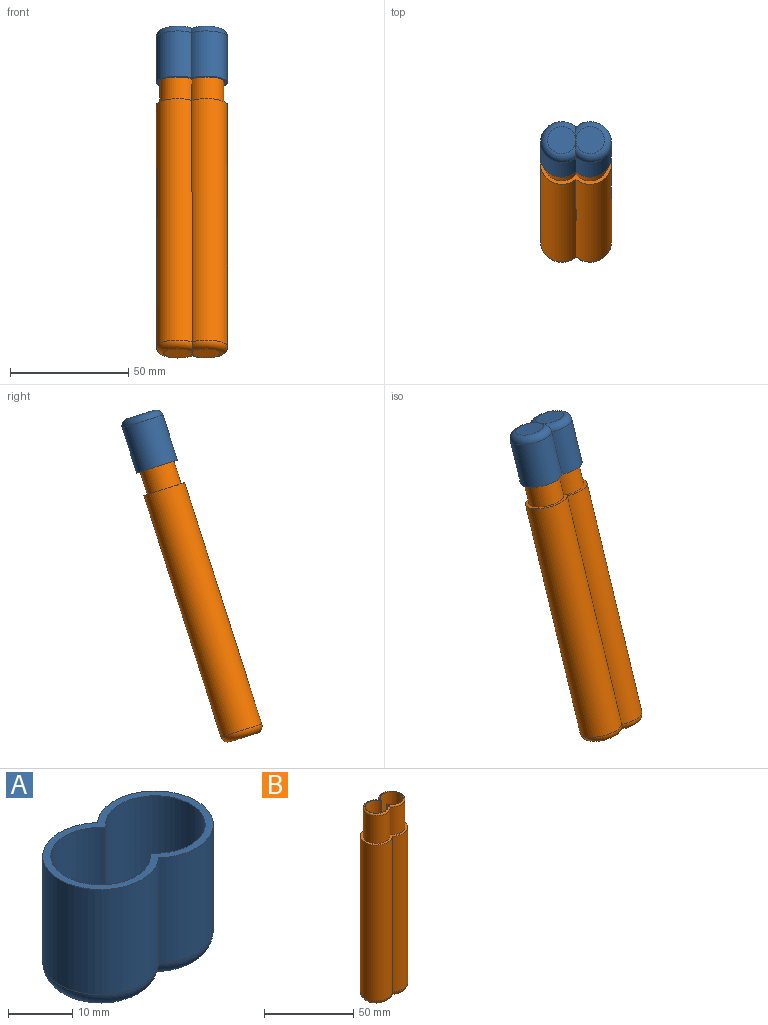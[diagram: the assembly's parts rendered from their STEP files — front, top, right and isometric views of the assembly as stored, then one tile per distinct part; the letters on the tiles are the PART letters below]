
ASSEMBLY  parts=2 mates=1
PART A: 10 faces, bbox 31.5x19.5x23 mm
  f0: plane 12x12mm, normal (0,0,-1), area 113.1mm2, adj f9
  f1: cylinder r=9mm len=20mm, axis (0,0,-1), area 828.2mm2, adj f2,f3,f9
  f2: cylinder r=9mm len=20mm, axis (0,0,-1), area 828.2mm2, adj f1,f3,f8
  f3: plane 30x18mm, normal (0,0,1), area 101.2mm2, adj f1,f2,f5,f6
  f4: plane 12x12mm, normal (0,0,-1), area 113.1mm2, adj f8
  f5: cylinder r=7.73mm len=20.5mm, axis (0,0,1), area 779.2mm2, adj f3,f6,f7
  f6: cylinder r=7.73mm len=20.5mm, axis (0,0,1), area 779.2mm2, adj f3,f5,f7
  f7: plane 27.45x15.45mm, normal (0,0,1), area 352mm2, adj f5,f6
  f8: torus R=6mm, axis (0,0,1), area 182.7mm2, adj f2,f4,f9
  f9: torus R=6mm, axis (0,0,1), area 182.7mm2, adj f0,f1,f8
PART B: 15 faces, bbox 31.5x19.5x130 mm
  f0: plane 12x12mm, normal (0,0,-1), area 113.1mm2, adj f14
  f1: cylinder r=9mm len=107mm, axis (0,0,-1), area 4430.8mm2, adj f2,f3,f14
  f2: cylinder r=9mm len=107mm, axis (0,0,-1), area 4430.8mm2, adj f1,f3,f13
  f3: plane 30x18mm, normal (0,0,1), area 118.1mm2, adj f1,f2,f5,f6
  f4: plane 12x12mm, normal (0,0,-1), area 113.1mm2, adj f13
  f5: cylinder r=7.5mm len=19mm, axis (0,0,-1), area 712mm2, adj f3,f6,f12
  f6: cylinder r=7.5mm len=19mm, axis (0,0,-1), area 712mm2, adj f3,f5,f11
  f7: plane 25x13mm, normal (0,0,1), area 14.3mm2, adj f8,f9,f11,f12
  f8: cylinder r=6.3mm len=128mm, axis (0,0,1), area 4567mm2, adj f7,f9,f10
  f9: cylinder r=6.3mm len=128mm, axis (0,0,1), area 4567mm2, adj f7,f8,f10
  f10: plane 24.6x12.6mm, normal (0,0,1), area 247.8mm2, adj f8,f9
  f11: torus R=6.5mm, axis (0,0,1), area 57.7mm2, adj f6,f7,f12
  f12: torus R=6.5mm, axis (0,0,1), area 57.7mm2, adj f5,f7,f11
  f13: torus R=6mm, axis (0,0,1), area 182.7mm2, adj f2,f4,f14
  f14: torus R=6mm, axis (0,0,1), area 182.7mm2, adj f0,f1,f13
PLACE A rot(axis=(0,0.99,-0.15),180deg) t=(16.36,-19.42,37.2)mm
PLACE B rot(axis=(-1,0,0),17.7deg) t=(16.41,-62.94,-99.02)mm
MATE slider B.f2 <-> A.f1  axis (0,0.3,0.95) through (22.36,-23.68,23.87)mm
